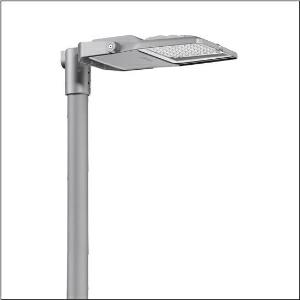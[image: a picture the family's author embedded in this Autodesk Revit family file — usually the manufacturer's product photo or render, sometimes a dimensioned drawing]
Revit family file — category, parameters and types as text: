
# Revit family: floodlight_fl_21_mini___pl64_5xa7776d2e3a_9c1a
name_source: partatom
category: Lighting Fixtures
units: mm (PartAtom-declared; Revit-internal decimal feet)

## family parameters
Cut with Voids When Loaded = No
Host = Face
Light Source = No
Part Type = Normal
Room Calculation Point = No
Round Connector Dimension = Use Diameter
Shared = No

## types (1)
- --- (1 x LED, 17220 lm, 142.9 W, 3000K)
    Apparent Load = 143 VA
    CIE Flux Codes = 28 80 98 100 100
    Color Rendering = 70
    Color Temperature = 3000K
    Default Elevation = 1800 mm
    Description = Floodlight FL 21 mini, floodlight, primary light control with lens, of PMMA, primary optical cover: protective disc, of toughened safety glass, transparent, light distribution: PL64, light emission: direct distribution, installation type: surface-mounted, LED, High Power LED, rated luminous flux: 17.220lm, luminous efficacy: 121lm/W, light colour: 730, colour temperature: 3000K, control: flexible luminous flux parameterisation, time-dependent luminous flux control, constant luminous flux control, overheat protection, presetting dimming logarithmic, with terminal, 6-pole, mains connection: 220..240V, AC, 50/60Hz, start of lifetime: 143W, end of service life: 151W, reduction: 63W, luminaire housing, of diecast aluminium, powder-coated, Siteco® metallic grey (DB 702S), corrosivity category C5 mid according to DIN EN ISO 12944, sealing non-destructively replaceable, please order mast flange separately, mast bracket, of steel, galvanised, powder-coated, Siteco® metallic grey (DB 702S), Smart Interface below and above, protection rating (complete): IP66, insulation class (complete): insulation class II (safety insulation), certification: CE, ENEC, VDE, protection symbol: D, impact resistance: IK08, permissible operating ambient temperature: -40..+40°C, permissible operating ambient temperature for outdoor applications: -40..+50°C, standard: DIN EN 12944, LABS conformity tested according to VDMA 24364:2018-05, packaging unit: 1 piece

Light Distribution: PL64
    Height = 70 mm
    Lamp = 1 x LED
    Lamp Light Flux = 17220 lm
    Lamp Power = 142.9 W
    Lamp count = 1
    Length = 485 mm
    Luminous efficacy = 121 lm/W
    Manufacturer = Siteco
    ModVariant = No
    Model = 5XA7776D2E3A
    Number of Poles = 1
    OnlyDefault = Yes
    Power Factor = 1
    Product Name = Floodlight FL 21 mini | PL64
    Product group = floodlight | pylon annexe
    ProductGroupID = 6200
    Protection Class = Protection class II
    Protection Degree = IP 66
    RLX_Detail_Level = 1
    RLX_Emergency_Light_Flux = 0 lm
    RLX_Emergency_Type = 0
    RLX_Emergency_Type_DB = No
    RlxData = <blob elided: 101393 chars, md5=45f96a91>
    Socket = socket
    Standby Power = 0 W
    System Light Flux = 17220 lm
    System Power = 143 W
    Type Comments = factory setting: luminous flux: 100 % | dim-lin: 254 | 730 mA
    Type Image = l_1007125.jpg
    URL = http://relux.com
    VarID = @adj_097503
    Voltage = 0 V
    Weight = 0.00 kg
    Width = 337 mm

## geometry (parser evidence)
native form markers: Blend x4, Sweep x12
no freeform markers — native parametric forms only
